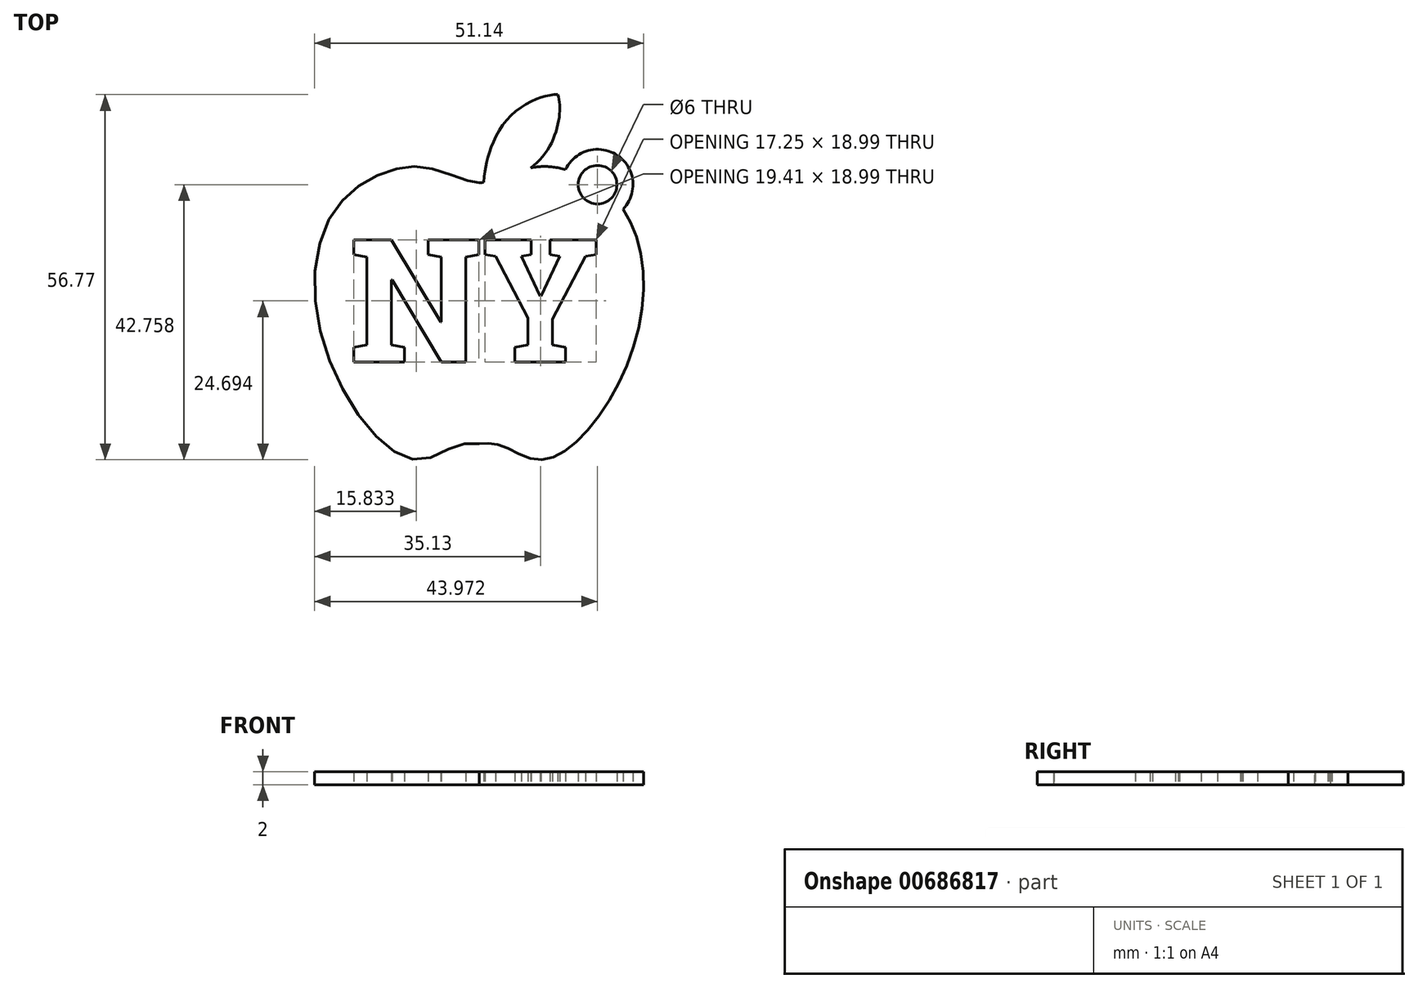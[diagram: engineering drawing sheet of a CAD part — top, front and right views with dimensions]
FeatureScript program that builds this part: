
annotation { "Feature Type Name" : "Feature", "Feature Type Description" : "" }
export const myFeature = defineFeature(function(context is Context, id is Id, definition is map)
    precondition{}
    {
        {
            var Q0;
            Q0=qCreatedBy(makeId("Top.planeOp"),FACE);
            var sketch = newSketch(context, id + "F0", { "sketchPlane" : qUnion([Q0])});
            skText(sketch, "E0", { "text": "NY\n", "fontName": "RobotoSlab-Bold.ttf"});
            skLineSegment(sketch, "E1", {"start": v(0, 0) * mm, "end": v(-29.76, 0) * mm, "construction": true});
            skLineSegment(sketch, "E2", {"start": v(0, 0) * mm, "end": v(29.76, 0) * mm, "construction": true});
            skFitSpline(sketch, "E3", {"points": [v(0, -21.54) * mm, v(-3.44, -21.85) * mm, v(-8.56, -23.99) * mm, v(-13.97, -22.24) * mm, v(-21.32, -12.86) * mm, v(-25.5, 1.23) * mm, v(-23.58, 12.78) * mm, v(-18.4, 18.7) * mm, v(-12.37, 21.3) * mm, v(-7.6, 21.22) * mm, v(-2.11, 19.45) * mm, v(0, 19.01) * mm], "startDerivative": vector(-51.07, 2.55) * mm, "endDerivative": vector(41.4, 0) * mm});
            skLineSegment(sketch, "E4", {"start": v(0, 19.01) * mm, "end": v(0, -21.54) * mm, "construction": true});
            skFitSpline(sketch, "E5.MirrorCS", {"points": [v(0, -21.54) * mm, v(3.44, -21.85) * mm, v(8.56, -23.99) * mm, v(13.97, -22.24) * mm, v(21.32, -12.86) * mm, v(25.5, 1.23) * mm, v(23.58, 12.78) * mm, v(18.4, 18.7) * mm, v(12.37, 21.3) * mm, v(7.6, 21.22) * mm, v(2.11, 19.45) * mm, v(0, 19.01) * mm], "startDerivative": vector(51.07, 2.55) * mm, "endDerivative": vector(-41.4, 0) * mm});
            skArc(sketch, "E6", {"start": v(22.35, 14.87) * mm, "mid": v(21.53, 23.22) * mm, "end": v(13.42, 21.04) * mm});
            skCircle(sketch, "E7", {"center": v(18.4, 18.7) * mm, "radius": 3 * mm});
            skLineSegment(sketch, "E8", {"start": v(2.11, 19.45) * mm, "end": v(12.25, 32.71) * mm, "construction": true});
            skFitSpline(sketch, "E9", {"points": [v(0.7, 19.01) * mm, v(1.45, 23.21) * mm, v(4.15, 28.63) * mm, v(9.11, 32.1) * mm, v(12.25, 32.71) * mm], "startDerivative": vector(1.45, 22.75) * mm, "endDerivative": vector(13.97, -0.37) * mm});
            skFitSpline(sketch, "E10.MirrorCS", {"points": [v(2.06, 17.98) * mm, v(5.92, 19.8) * mm, v(10.43, 23.83) * mm, v(12.48, 29.52) * mm, v(12.25, 32.71) * mm], "startDerivative": vector(21.56, 7.38) * mm, "endDerivative": vector(-4.03, 13.38) * mm});
            const initialGuessF0  = {"E0": [-0.02017, -0.00886, 1, 0, 0.01923]};
            skSetInitialGuess(sketch, initialGuessF0);
            skSolve(sketch);
        }
        {
            var Q0;
            Q0 = qSketchRegion(id + "F0", true);
            extrude(context, id + "F1", {"entities" : qUnion([Q0]), "depth" : 2 * mm, "offsetDistance" : 25 * mm});
        }
    });
